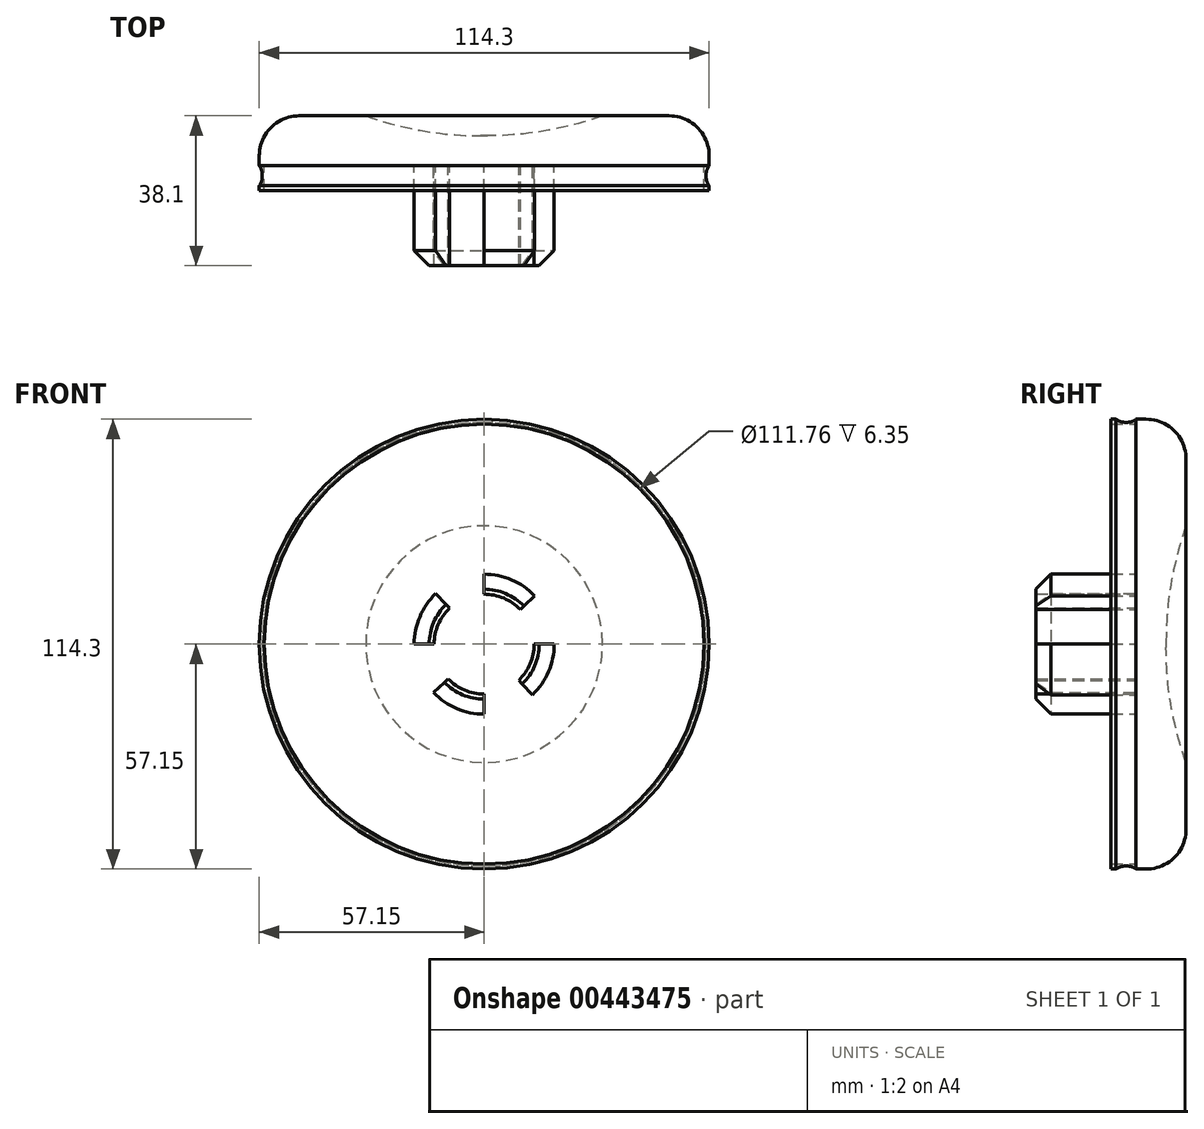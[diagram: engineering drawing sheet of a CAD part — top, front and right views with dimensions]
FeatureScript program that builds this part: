
annotation { "Feature Type Name" : "Feature", "Feature Type Description" : "" }
export const myFeature = defineFeature(function(context is Context, id is Id, definition is map)
    precondition{}
    {
        {
            var Q0;
            Q0=qCreatedBy(makeId("Front.planeOp"),FACE);
            var sketch = newSketch(context, id + "F0", { "sketchPlane" : qUnion([Q0])});
            skPoint(sketch, "E0.center.orphan", {"position": v(1.96, 0) * mm});
            skCircle(sketch, "E1", {"center": v(0, 0) * mm, "radius": 57.15 * mm});
            skCircle(sketch, "E2", {"center": v(0, 0) * mm, "radius": 54.61 * mm});
            skSolve(sketch);
        }
        {
            var Q0;
            Q0=makeQuery(id+"F0.imprint","IMPRINT",FACE,{"disambiguationData":[TD([[makeQuery(id+"F0.imprint","IMPRINT",EDGE,{"derivedFrom":sQuery(id+"F0.wireOp",EDGE,"E0")}),1.0]])]});
            var Q1;
            Q1=makeQuery(id+"F0.imprint","IMPRINT",FACE,{"disambiguationData":[TD([[makeQuery(id+"F0.imprint","IMPRINT",EDGE,{"derivedFrom":sQuery(id+"F0.wireOp",EDGE,"E2")}),1.0]])]});
            var Q2;
            Q2=makeQuery(id+"F0.imprint","IMPRINT",FACE,{"disambiguationData":[TD([[makeQuery(id+"F0.imprint","IMPRINT",EDGE,{"derivedFrom":sQuery(id+"F0.wireOp",EDGE,"E1")}),1.0]])]});
            extrude(context, id + "F1", {"entities" : qUnion([Q0, Q1, Q2]), "depth" : 12.7 * mm});
        }
        {
            var Q0;
            Q0=makeQuery(id+"F1.opExtrude","CAP_FACE",FACE,{"disambiguationData":[OSD([sQuery(id+"F0.wireOp",EDGE,"E1")])],"isStart":false});
            var sketch = newSketch(context, id + "F2", { "sketchPlane" : qUnion([Q0])});
            skCircle(sketch, "E3", {"center": v(0, 0) * mm, "radius": 55.88 * mm});
            skSolve(sketch);
        }
        {
            var Q0;
            Q0=makeQuery(id+"F2.imprint","IMPRINT",FACE,{"disambiguationData":[TD([[makeQuery(id+"F2.imprint","IMPRINT",EDGE,{"derivedFrom":sQuery(id+"F2.wireOp",EDGE,"E3")}),-1.0]])]});
            extrude(context, id + "F3", {"entities" : qUnion([Q0]), "operationType" : NewBodyOperationType.ADD, "depth" : 6.35 * mm});
        }
        {
            var Q0;
            Q0=makeQuery(id+"F1.opExtrude","CAP_FACE",FACE,{"disambiguationData":[OSD([sQuery(id+"F0.wireOp",EDGE,"E1")])],"isStart":false});
            var sketch = newSketch(context, id + "F4", { "sketchPlane" : qUnion([Q0])});
            skCircle(sketch, "E4", {"center": v(0, 0) * mm, "radius": 17.78 * mm});
            skCircle(sketch, "E5", {"center": v(0, 0) * mm, "radius": 12.7 * mm});
            skLineSegment(sketch, "E6", {"start": v(0, 0) * mm, "end": v(0, 17.78) * mm});
            skLineSegment(sketch, "E7", {"start": v(0, 0) * mm, "end": v(12.84, 12.3) * mm});
            skLineSegment(sketch, "E8", {"start": v(0, 0) * mm, "end": v(17.78, 0) * mm});
            skLineSegment(sketch, "E9", {"start": v(0, 0) * mm, "end": v(12.3, -12.84) * mm});
            skLineSegment(sketch, "E10", {"start": v(0, 0) * mm, "end": v(0, -17.78) * mm});
            skLineSegment(sketch, "E11", {"start": v(0, 0) * mm, "end": v(-12.84, -12.3) * mm});
            skLineSegment(sketch, "E12", {"start": v(0, 0) * mm, "end": v(-17.78, 0) * mm});
            skLineSegment(sketch, "E13", {"start": v(0, 0) * mm, "end": v(-12.3, 12.84) * mm});
            skSolve(sketch);
        }
        {
            var Q0;
            {var subQ0=sQuery(id+"F4.wireOp",EDGE,"E6");var subQ1=sQuery(id+"F4.wireOp",EDGE,"E4");var subQ2=makeQuery(id+"F4.imprint","INTERSECT",VERTEX,{"derivedFrom":[subQ1,subQ0]});Q0=makeQuery(id+"F4.imprint","IMPRINT",FACE,{"disambiguationData":[TD([[makeQuery(id+"F4.imprint","IMPRINT",EDGE,{"disambiguationData":[TD([[subQ2,1.0]])],"derivedFrom":subQ1}),1.0]])]});}
            var Q1;
            {var subQ0=sQuery(id+"F4.wireOp",EDGE,"E8");var subQ1=sQuery(id+"F4.wireOp",EDGE,"E4");var subQ2=makeQuery(id+"F4.imprint","INTERSECT",VERTEX,{"derivedFrom":[subQ1,subQ0]});Q1=makeQuery(id+"F4.imprint","IMPRINT",FACE,{"disambiguationData":[TD([[makeQuery(id+"F4.imprint","IMPRINT",EDGE,{"disambiguationData":[TD([[subQ2,1.0]])],"derivedFrom":subQ1}),1.0]])]});}
            var Q2;
            {var subQ0=sQuery(id+"F4.wireOp",EDGE,"E10");var subQ1=sQuery(id+"F4.wireOp",EDGE,"E4");var subQ2=makeQuery(id+"F4.imprint","INTERSECT",VERTEX,{"derivedFrom":[subQ1,subQ0]});Q2=makeQuery(id+"F4.imprint","IMPRINT",FACE,{"disambiguationData":[TD([[makeQuery(id+"F4.imprint","IMPRINT",EDGE,{"disambiguationData":[TD([[subQ2,1.0]])],"derivedFrom":subQ1}),1.0]])]});}
            var Q3;
            {var subQ0=sQuery(id+"F4.wireOp",EDGE,"E12");var subQ1=sQuery(id+"F4.wireOp",EDGE,"E4");var subQ2=makeQuery(id+"F4.imprint","INTERSECT",VERTEX,{"derivedFrom":[subQ1,subQ0]});Q3=makeQuery(id+"F4.imprint","IMPRINT",FACE,{"disambiguationData":[TD([[makeQuery(id+"F4.imprint","IMPRINT",EDGE,{"disambiguationData":[TD([[subQ2,1.0]])],"derivedFrom":subQ1}),1.0]])]});}
            extrude(context, id + "F5", {"entities" : qUnion([Q0, Q1, Q2, Q3]), "operationType" : NewBodyOperationType.ADD, "depth" : 25.4 * mm});
        }
        {
            var Q0;
            Q0=makeQuery(id+"F1.opExtrude","CAP_EDGE",EDGE,{"disambiguationData":[OSD([sQuery(id+"F0.wireOp",EDGE,"E1")])],"isStart":true});
            fillet(context, id + "F6", {"entities" : qUnion([Q0]), "radius" : 10.16 * mm, "tangentPropagation" : true, "allowEdgeOverflow" : false});
        }
        {
            var Q0;
            Q0=qCreatedBy(makeId("Front.planeOp"),FACE);
            cPlane(context, id + "F7", {"entities" : qUnion([Q0]), "cplaneType" : CPlaneType.OFFSET, "offset" : 12.7 * mm, "width" : 152.4 * mm, "height" : 152.4 * mm});
        }
        {
            var Q0;
            Q0=qCreatedBy(id+"F7.planeOp",FACE);
            var sketch = newSketch(context, id + "F8", { "sketchPlane" : qUnion([Q0])});
            skCircle(sketch, "E14", {"center": v(0, 0) * mm, "radius": 57.36 * mm});
            skCircle(sketch, "E15", {"center": v(0, 0) * mm, "radius": 56.38 * mm});
            skSolve(sketch);
        }
        {
            var Q0;
            Q0 = qSketchRegion(id + "F8", true);
            extrude(context, id + "F9", {"entities" : qUnion([Q0]), "operationType" : NewBodyOperationType.REMOVE, "depth" : 5.08 * mm, "offsetDistance" : 25.4 * mm});
        }
        {
            var Q0;
            Q0=makeQuery(id+"F9.boolean.opBoolean","COPY",FACE,{"derivedFrom":makeQuery(id+"F9.opExtrude","SWEPT_FACE",FACE,{"disambiguationData":[OSD([sQuery(id+"F8.wireOp",EDGE,"E15")])]})});
            fillet(context, id + "F10", {"entities" : qUnion([Q0]), "radius" : 3.8 * mm, "tangentPropagation" : true, "allowEdgeOverflow" : false});
        }
        {
            var Q0;
            {var subQ0=sQuery(id+"F4.wireOp",EDGE,"E4");Q0=makeQuery(id+"F5.opExtrude","CAP_EDGE",EDGE,{"disambiguationData":[OSD([subQ0]),TDD([makeQuery(id+"F4.imprint","IMPRINT",EDGE,{"disambiguationData":[TD([[makeQuery(id+"F4.imprint","INTERSECT",VERTEX,{"derivedFrom":[subQ0,sQuery(id+"F4.wireOp",EDGE,"E12")]}),1.0]])],"derivedFrom":subQ0})])],"isStart":false});}
            var Q1;
            {var subQ0=sQuery(id+"F4.wireOp",EDGE,"E4");Q1=makeQuery(id+"F5.opExtrude","CAP_EDGE",EDGE,{"disambiguationData":[OSD([subQ0]),TDD([makeQuery(id+"F4.imprint","IMPRINT",EDGE,{"disambiguationData":[TD([[makeQuery(id+"F4.imprint","INTERSECT",VERTEX,{"derivedFrom":[subQ0,sQuery(id+"F4.wireOp",EDGE,"E10")]}),1.0]])],"derivedFrom":subQ0})])],"isStart":false});}
            var Q2;
            {var subQ0=sQuery(id+"F4.wireOp",EDGE,"E4");Q2=makeQuery(id+"F5.opExtrude","CAP_EDGE",EDGE,{"disambiguationData":[OSD([subQ0]),TDD([makeQuery(id+"F4.imprint","IMPRINT",EDGE,{"disambiguationData":[TD([[makeQuery(id+"F4.imprint","INTERSECT",VERTEX,{"derivedFrom":[subQ0,sQuery(id+"F4.wireOp",EDGE,"E8")]}),1.0]])],"derivedFrom":subQ0})])],"isStart":false});}
            var Q3;
            {var subQ0=sQuery(id+"F4.wireOp",EDGE,"E4");Q3=makeQuery(id+"F5.opExtrude","CAP_EDGE",EDGE,{"disambiguationData":[OSD([subQ0]),TDD([makeQuery(id+"F4.imprint","IMPRINT",EDGE,{"disambiguationData":[TD([[makeQuery(id+"F4.imprint","INTERSECT",VERTEX,{"derivedFrom":[subQ0,sQuery(id+"F4.wireOp",EDGE,"E6")]}),1.0]])],"derivedFrom":subQ0})])],"isStart":false});}
            chamfer(context, id + "F11", {"entities" : qUnion([Q0, Q1, Q2, Q3]), "width" : 3.8 * mm, "tangentPropagation" : true});
        }
        {
            var Q0;
            Q0=makeQuery(id+"F1.opExtrude","CAP_FACE",FACE,{"disambiguationData":[OSD([sQuery(id+"F0.wireOp",EDGE,"E1")])],"isStart":true});
            var sketch = newSketch(context, id + "F12", { "sketchPlane" : qUnion([Q0])});
            skCircle(sketch, "E16", {"center": v(0, 0) * mm, "radius": 30.07 * mm});
            skSolve(sketch);
        }
        {
            var Q0;
            Q0=makeQuery(id+"F12.imprint","IMPRINT",FACE,{"disambiguationData":[TD([[makeQuery(id+"F12.imprint","IMPRINT",EDGE,{"derivedFrom":sQuery(id+"F12.wireOp",EDGE,"E16")}),1.0]])]});
            extrude(context, id + "F13", {"entities" : qUnion([Q0]), "operationType" : NewBodyOperationType.REMOVE, "oppositeDirection" : true, "depth" : 5.08 * mm, "offsetDistance" : 25.4 * mm});
        }
        {
            var Q0;
            Q0=makeQuery(id+"F13.boolean.opBoolean","COPY",EDGE,{"derivedFrom":makeQuery(id+"F13.opExtrude","CAP_EDGE",EDGE,{"disambiguationData":[OSD([sQuery(id+"F12.wireOp",EDGE,"E16")])],"isStart":false})});
            fillet(context, id + "F14", {"entities" : qUnion([Q0]), "radius" : 86.36 * mm, "tangentPropagation" : true, "allowEdgeOverflow" : false});
        }
    });
